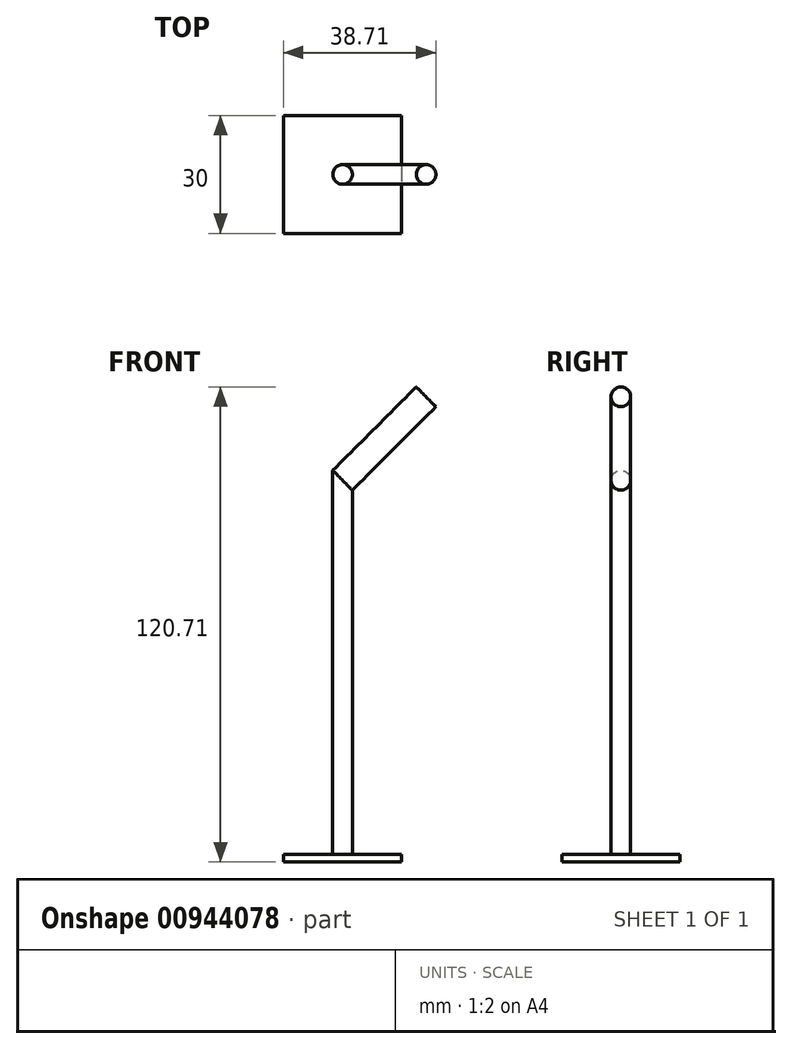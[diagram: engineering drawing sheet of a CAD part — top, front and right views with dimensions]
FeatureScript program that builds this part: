
annotation { "Feature Type Name" : "Feature", "Feature Type Description" : "" }
export const myFeature = defineFeature(function(context is Context, id is Id, definition is map)
    precondition{}
    {
        {
            var Q0;
            Q0=qCreatedBy(makeId("Top.planeOp"),FACE);
            var sketch = newSketch(context, id + "F0", { "sketchPlane" : qUnion([Q0])});
            skLineSegment(sketch, "E0.bottom", {"start": v(15, 15) * mm, "end": v(-15, 15) * mm});
            skLineSegment(sketch, "E0.top", {"start": v(15, -15) * mm, "end": v(-15, -15) * mm});
            skLineSegment(sketch, "E0.left", {"start": v(15, 15) * mm, "end": v(15, -15) * mm});
            skLineSegment(sketch, "E0.right", {"start": v(-15, 15) * mm, "end": v(-15, -15) * mm});
            skPoint(sketch, "E0.middle", {"position": v(0, 0) * mm});
            skCircle(sketch, "E1", {"center": v(0, 0) * mm, "radius": 2.5 * mm});
            skSolve(sketch);
        }
        {
            var Q0;
            Q0=makeQuery(id+"F0.imprint","IMPRINT",FACE,{"disambiguationData":[TD([[makeQuery(id+"F0.imprint","IMPRINT",EDGE,{"derivedFrom":sQuery(id+"F0.wireOp",EDGE,"E0.bottom")}),1.0]])]});
            extrude(context, id + "F1", {"entities" : qUnion([Q0]), "depth" : 2 * mm, "offsetDistance" : 25 * mm});
        }
        {
            var Q0;
            Q0=makeQuery(id+"F0.imprint","IMPRINT",FACE,{"disambiguationData":[TD([[makeQuery(id+"F0.imprint","IMPRINT",EDGE,{"derivedFrom":sQuery(id+"F0.wireOp",EDGE,"E1")}),1.0]])]});
            extrude(context, id + "F2", {"entities" : qUnion([Q0]), "operationType" : NewBodyOperationType.ADD, "depth" : 100 * mm, "offsetDistance" : 25 * mm});
        }
        {
            var Q0;
            Q0=qCreatedBy(makeId("Front.planeOp"),FACE);
            var sketch = newSketch(context, id + "F3", { "sketchPlane" : qUnion([Q0])});
            skLineSegment(sketch, "E2.bottom", {"start": v(-3, 0) * mm, "end": v(3, 0) * mm});
            skLineSegment(sketch, "E2.top", {"start": v(-3, 100) * mm, "end": v(3, 100) * mm});
            skLineSegment(sketch, "E2.left", {"start": v(-3, 0) * mm, "end": v(-3, 100) * mm});
            skLineSegment(sketch, "E2.right", {"start": v(3, 0) * mm, "end": v(3, 100) * mm});
            skLineSegment(sketch, "E3", {"start": v(-3, 100) * mm, "end": v(3, 94) * mm});
            skSolve(sketch);
        }
        {
            var Q0;
            {var subQ0=sQuery(id+"F3.wireOp",EDGE,"E2.top");Q0=makeQuery(id+"F3.imprint","IMPRINT",FACE,{"disambiguationData":[TD([[makeQuery(id+"F3.imprint","IMPRINT",EDGE,{"derivedFrom":subQ0}),-1.0]])]});}
            extrude(context, id + "F4", {"entities" : qUnion([Q0]), "operationType" : NewBodyOperationType.REMOVE, "endBound" : BoundingType.SYMMETRIC, "oppositeDirection" : true, "depth" : 25 * mm, "offsetDistance" : 25 * mm});
        }
        {
            var Q0;
            Q0=makeQuery(id+"F4.boolean.opBoolean","COPY",FACE,{"derivedFrom":makeQuery(id+"F4.opExtrude","SWEPT_FACE",FACE,{"disambiguationData":[OSD([sQuery(id+"F3.wireOp",EDGE,"E3")])]})});
            extrude(context, id + "F5", {"entities" : qUnion([Q0]), "operationType" : NewBodyOperationType.ADD, "depth" : 30 * mm, "offsetDistance" : 25 * mm});
        }
    });
